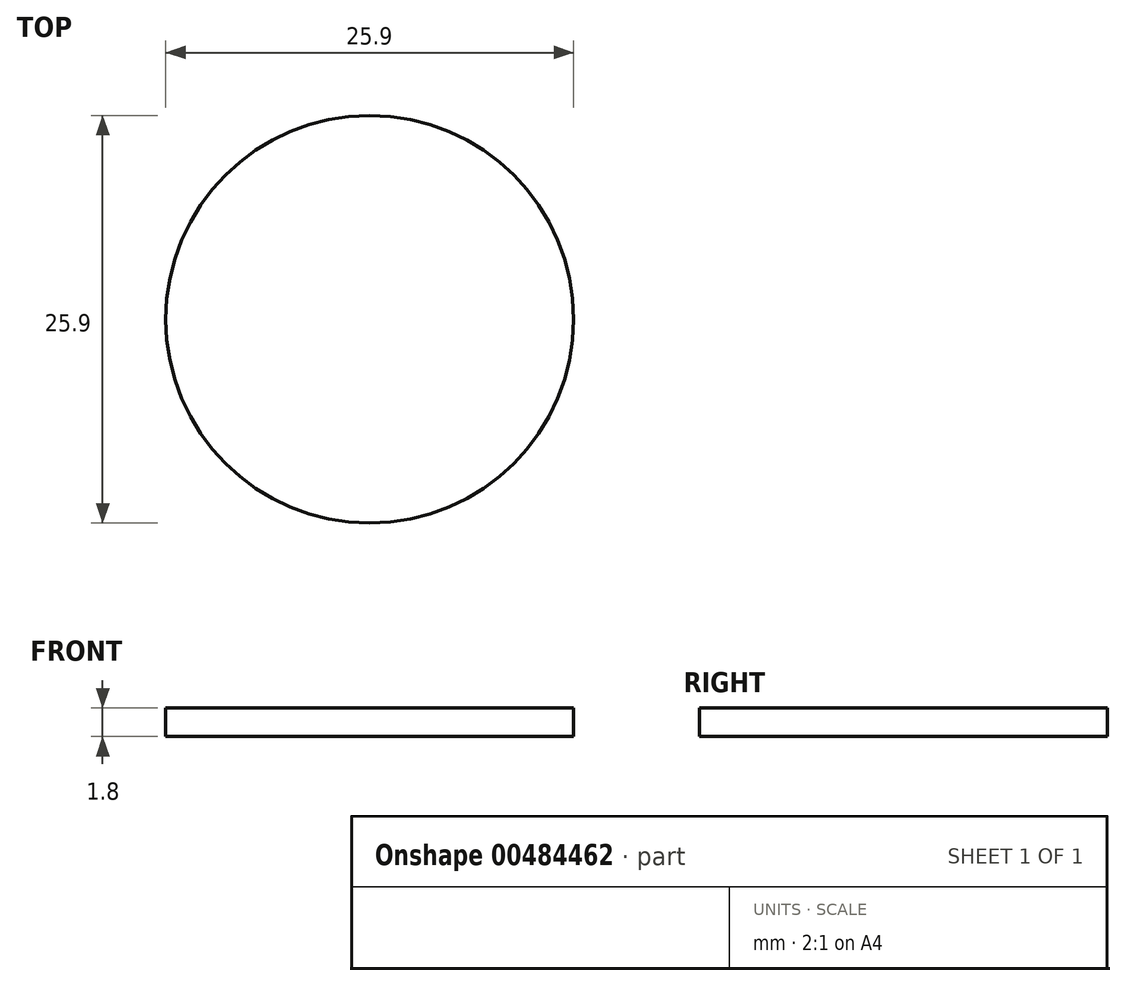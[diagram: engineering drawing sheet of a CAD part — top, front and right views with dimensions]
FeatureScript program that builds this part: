
annotation { "Feature Type Name" : "Feature", "Feature Type Description" : "" }
export const myFeature = defineFeature(function(context is Context, id is Id, definition is map)
    precondition{}
    {
        {
            var Q0;
            Q0=qCreatedBy(makeId("Top.planeOp"),FACE);
            var sketch = newSketch(context, id + "F0", { "sketchPlane" : qUnion([Q0])});
            skCircle(sketch, "E0", {"center": v(0, 0) * mm, "radius": 12.95 * mm});
            skSolve(sketch);
        }
        {
            var Q0;
            Q0=makeQuery(id+"F0.imprint","IMPRINT",FACE,{"disambiguationData":[TD([[makeQuery(id+"F0.imprint","IMPRINT",EDGE,{"derivedFrom":sQuery(id+"F0.wireOp",EDGE,"E0")}),1.0]])]});
            extrude(context, id + "F1", {"entities" : qUnion([Q0]), "depth" : 1.8 * mm, "offsetDistance" : 25 * mm});
        }
    });
